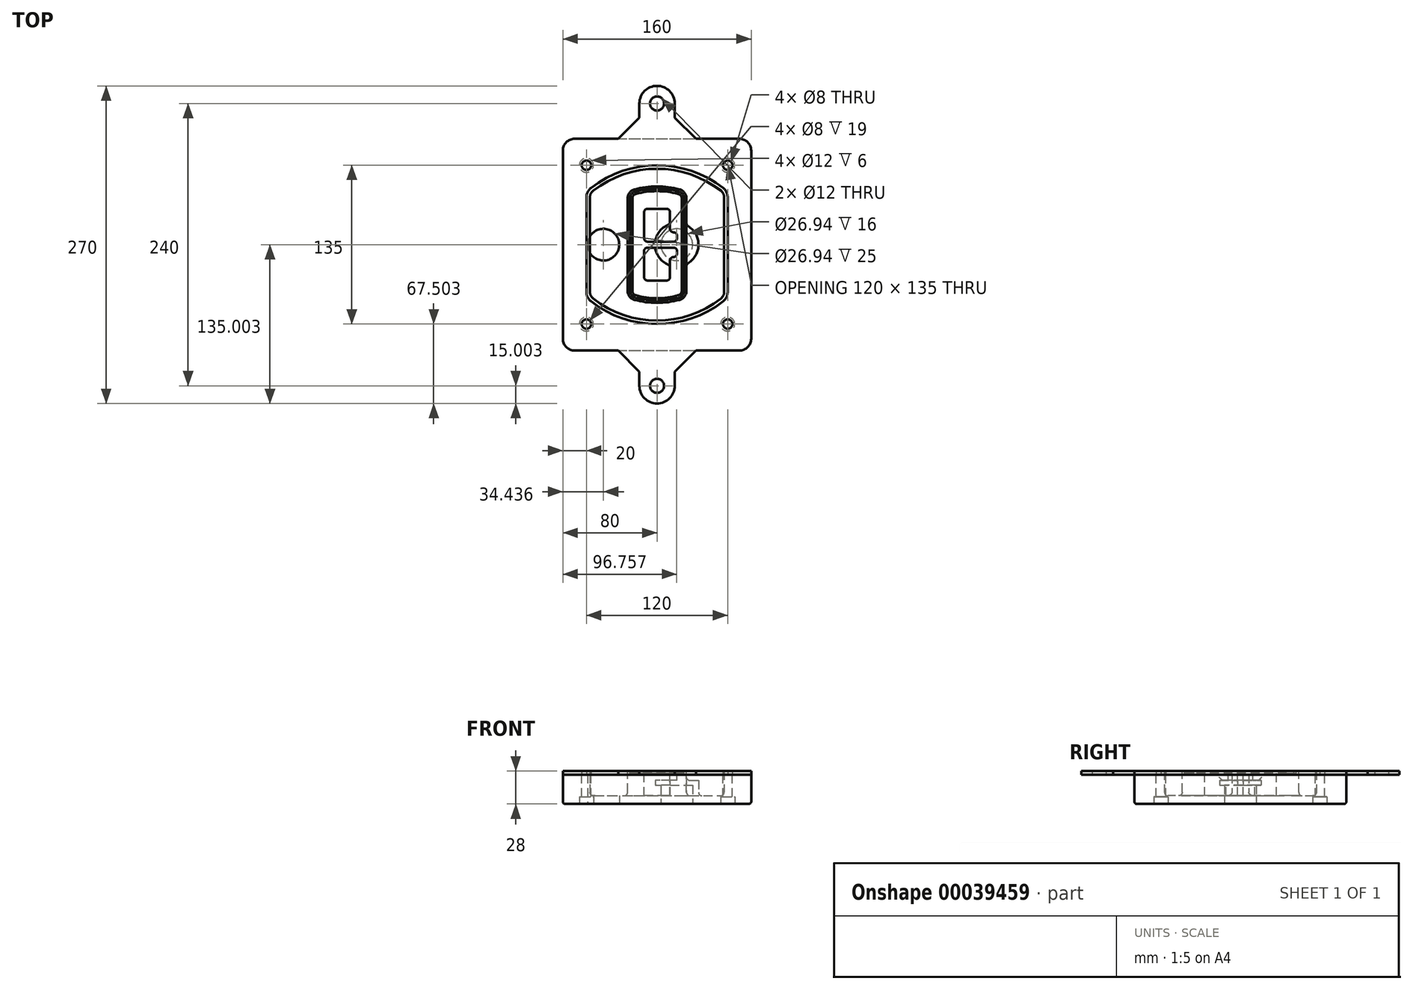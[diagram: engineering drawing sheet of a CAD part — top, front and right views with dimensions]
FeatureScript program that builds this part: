
annotation { "Feature Type Name" : "Feature", "Feature Type Description" : "" }
export const myFeature = defineFeature(function(context is Context, id is Id, definition is map)
    precondition{}
    {
        {
            var Q0;
            Q0=qCreatedBy(makeId("Top.planeOp"),FACE);
            var sketch = newSketch(context, id + "F0", { "sketchPlane" : qUnion([Q0])});
            skPoint(sketch, "E0.rect.middle", {"position": v(0, 0) * mm});
            skLineSegment(sketch, "E1.bottom", {"start": v(24.05, 28.38) * mm, "end": v(164.05, 28.38) * mm});
            skLineSegment(sketch, "E1.top", {"start": v(24.05, 208.38) * mm, "end": v(164.05, 208.38) * mm});
            skLineSegment(sketch, "E1.left", {"start": v(14.05, 38.38) * mm, "end": v(14.05, 198.38) * mm});
            skLineSegment(sketch, "E1.right", {"start": v(174.05, 38.38) * mm, "end": v(174.05, 198.38) * mm});
            skLineSegment(sketch, "E2", {"start": v(14.05, 208.38) * mm, "end": v(174.05, 28.38) * mm, "construction": true});
            skLineSegment(sketch, "E3", {"start": v(174.05, 208.38) * mm, "end": v(14.05, 28.38) * mm, "construction": true});
            skCircle(sketch, "E4", {"center": v(34.05, 185.88) * mm, "radius": 4 * mm});
            skCircle(sketch, "E5", {"center": v(154.05, 185.88) * mm, "radius": 4 * mm});
            skCircle(sketch, "E6", {"center": v(154.05, 50.88) * mm, "radius": 4 * mm});
            skCircle(sketch, "E7", {"center": v(34.05, 50.88) * mm, "radius": 4 * mm});
            skLineSegment(sketch, "E8", {"start": v(34.05, 185.88) * mm, "end": v(154.05, 185.88) * mm, "construction": true});
            skLineSegment(sketch, "E9", {"start": v(154.05, 185.88) * mm, "end": v(154.05, 50.88) * mm, "construction": true});
            skLineSegment(sketch, "E10", {"start": v(154.05, 50.88) * mm, "end": v(34.05, 50.88) * mm, "construction": true});
            skLineSegment(sketch, "E11", {"start": v(34.05, 50.88) * mm, "end": v(34.05, 185.88) * mm, "construction": true});
            skLineSegment(sketch, "E12", {"start": v(34.05, 158.68) * mm, "end": v(34.05, 78.09) * mm});
            skLineSegment(sketch, "E13", {"start": v(154.05, 158.68) * mm, "end": v(154.05, 78.09) * mm});
            skArc(sketch, "E14", {"start": v(150.2, 166.56) * mm, "mid": v(94.05, 185.88) * mm, "end": v(37.9, 166.56) * mm});
            skArc(sketch, "E15", {"start": v(37.9, 70.2) * mm, "mid": v(94.05, 50.88) * mm, "end": v(150.2, 70.2) * mm});
            skLineSegment(sketch, "E16", {"start": v(34.05, 118.38) * mm, "end": v(154.05, 118.38) * mm, "construction": true});
            skPoint(sketch, "E17.visualSharp", {"position": v(34.05, 73.38) * mm});
            skArc(sketch, "E17.filletArc", {"start": v(34.05, 78.09) * mm, "mid": v(35.06, 73.7) * mm, "end": v(37.9, 70.2) * mm});
            skPoint(sketch, "E18.visualSharp", {"position": v(34.05, 163.38) * mm});
            skArc(sketch, "E18.filletArc", {"start": v(37.9, 166.56) * mm, "mid": v(35.06, 163.06) * mm, "end": v(34.05, 158.68) * mm});
            skPoint(sketch, "E19.visualSharp", {"position": v(154.05, 163.38) * mm});
            skArc(sketch, "E19.filletArc", {"start": v(154.05, 158.68) * mm, "mid": v(153.04, 163.06) * mm, "end": v(150.2, 166.56) * mm});
            skPoint(sketch, "E20.visualSharp", {"position": v(154.05, 73.38) * mm});
            skArc(sketch, "E20.filletArc", {"start": v(150.2, 70.2) * mm, "mid": v(153.04, 73.7) * mm, "end": v(154.05, 78.09) * mm});
            skPoint(sketch, "E21.visualSharp", {"position": v(14.05, 208.38) * mm});
            skArc(sketch, "E21.filletArc", {"start": v(24.05, 208.38) * mm, "mid": v(16.98, 205.45) * mm, "end": v(14.05, 198.38) * mm});
            skPoint(sketch, "E22.visualSharp", {"position": v(174.05, 208.38) * mm});
            skArc(sketch, "E22.filletArc", {"start": v(174.05, 198.38) * mm, "mid": v(171.12, 205.45) * mm, "end": v(164.05, 208.38) * mm});
            skPoint(sketch, "E23.visualSharp", {"position": v(174.05, 28.38) * mm});
            skArc(sketch, "E23.filletArc", {"start": v(164.05, 28.38) * mm, "mid": v(171.12, 31.31) * mm, "end": v(174.05, 38.38) * mm});
            skPoint(sketch, "E24.visualSharp", {"position": v(14.05, 28.38) * mm});
            skArc(sketch, "E24.filletArc", {"start": v(14.05, 38.38) * mm, "mid": v(16.98, 31.31) * mm, "end": v(24.05, 28.38) * mm});
            skArc(sketch, "E25.0", {"start": v(151.05, 158.68) * mm, "mid": v(150.34, 161.75) * mm, "end": v(148.36, 164.2) * mm});
            skLineSegment(sketch, "E25.1", {"start": v(151.05, 158.68) * mm, "end": v(151.05, 78.09) * mm});
            skArc(sketch, "E25.2", {"start": v(148.36, 72.57) * mm, "mid": v(150.34, 75.02) * mm, "end": v(151.05, 78.09) * mm});
            skArc(sketch, "E25.3", {"start": v(39.74, 72.57) * mm, "mid": v(94.05, 53.88) * mm, "end": v(148.36, 72.57) * mm});
            skArc(sketch, "E25.4", {"start": v(37.05, 78.09) * mm, "mid": v(37.76, 75.02) * mm, "end": v(39.74, 72.57) * mm});
            skArc(sketch, "E25.5", {"start": v(148.36, 164.2) * mm, "mid": v(94.05, 182.88) * mm, "end": v(39.74, 164.2) * mm});
            skLineSegment(sketch, "E25.6", {"start": v(37.05, 158.68) * mm, "end": v(37.05, 78.09) * mm});
            skArc(sketch, "E25.7", {"start": v(39.74, 164.2) * mm, "mid": v(37.76, 161.75) * mm, "end": v(37.05, 158.68) * mm});
            skArc(sketch, "E26.0", {"start": v(35.43, 169.71) * mm, "mid": v(31.47, 164.82) * mm, "end": v(30.05, 158.68) * mm});
            skArc(sketch, "E26.1", {"start": v(152.67, 169.71) * mm, "mid": v(94.05, 189.88) * mm, "end": v(35.43, 169.71) * mm});
            skArc(sketch, "E26.2", {"start": v(158.05, 158.68) * mm, "mid": v(156.63, 164.82) * mm, "end": v(152.67, 169.71) * mm});
            skLineSegment(sketch, "E26.3", {"start": v(158.05, 158.68) * mm, "end": v(158.05, 78.09) * mm});
            skArc(sketch, "E26.4", {"start": v(152.67, 67.05) * mm, "mid": v(156.63, 71.95) * mm, "end": v(158.05, 78.09) * mm});
            skLineSegment(sketch, "E26.5", {"start": v(30.05, 158.68) * mm, "end": v(30.05, 78.09) * mm});
            skArc(sketch, "E26.6", {"start": v(35.43, 67.05) * mm, "mid": v(94.05, 46.88) * mm, "end": v(152.67, 67.05) * mm});
            skArc(sketch, "E26.7", {"start": v(30.05, 78.09) * mm, "mid": v(31.47, 71.95) * mm, "end": v(35.43, 67.05) * mm});
            skSolve(sketch);
        }
        {
            var Q0;
            Q0=makeQuery(id+"F0.imprint","IMPRINT",FACE,{"disambiguationData":[TD([[makeQuery(id+"F0.imprint","IMPRINT",EDGE,{"derivedFrom":sQuery(id+"F0.wireOp",EDGE,"E1.bottom")}),1.0]])]});
            var Q1;
            Q1=makeQuery(id+"F0.imprint","IMPRINT",FACE,{"disambiguationData":[TD([[makeQuery(id+"F0.imprint","IMPRINT",EDGE,{"derivedFrom":sQuery(id+"F0.wireOp",EDGE,"E12")}),1.0]])]});
            var Q2;
            Q2=makeQuery(id+"F0.imprint","IMPRINT",FACE,{"disambiguationData":[TD([[makeQuery(id+"F0.imprint","IMPRINT",EDGE,{"derivedFrom":sQuery(id+"F0.wireOp",EDGE,"E25.0")}),1.0]])]});
            var Q3;
            Q3=makeQuery(id+"F0.imprint","IMPRINT",FACE,{"disambiguationData":[TD([[makeQuery(id+"F0.imprint","IMPRINT",EDGE,{"derivedFrom":sQuery(id+"F0.wireOp",EDGE,"E12")}),-1.0]])]});
            extrude(context, id + "F1", {"entities" : qUnion([Q0, Q1, Q2, Q3]), "oppositeDirection" : true, "depth" : 25 * mm});
        }
        {
            var Q0;
            Q0=makeQuery(id+"F0.imprint","IMPRINT",FACE,{"disambiguationData":[TD([[makeQuery(id+"F0.imprint","IMPRINT",EDGE,{"derivedFrom":sQuery(id+"F0.wireOp",EDGE,"E12")}),1.0]])]});
            extrude(context, id + "F2", {"entities" : qUnion([Q0]), "operationType" : NewBodyOperationType.ADD, "depth" : 3 * mm});
        }
        {
            var Q0;
            Q0=makeQuery(id+"F0.imprint","IMPRINT",FACE,{"disambiguationData":[TD([[makeQuery(id+"F0.imprint","IMPRINT",EDGE,{"derivedFrom":sQuery(id+"F0.wireOp",EDGE,"E25.0")}),1.0]])]});
            extrude(context, id + "F3", {"entities" : qUnion([Q0]), "operationType" : NewBodyOperationType.REMOVE, "oppositeDirection" : true, "depth" : 18 * mm});
        }
        {
            var Q0;
            Q0=makeQuery(id+"F2.opExtrude","CAP_FACE",FACE,{"disambiguationData":[OSD([sQuery(id+"F0.wireOp",EDGE,"E12"),sQuery(id+"F0.wireOp",EDGE,"E13"),sQuery(id+"F0.wireOp",EDGE,"E14"),sQuery(id+"F0.wireOp",EDGE,"E15"),sQuery(id+"F0.wireOp",EDGE,"E17.filletArc"),sQuery(id+"F0.wireOp",EDGE,"E18.filletArc"),sQuery(id+"F0.wireOp",EDGE,"E19.filletArc"),sQuery(id+"F0.wireOp",EDGE,"E20.filletArc"),sQuery(id+"F0.wireOp",EDGE,"E25.0"),sQuery(id+"F0.wireOp",EDGE,"E25.1"),sQuery(id+"F0.wireOp",EDGE,"E25.2"),sQuery(id+"F0.wireOp",EDGE,"E25.3"),sQuery(id+"F0.wireOp",EDGE,"E25.4"),sQuery(id+"F0.wireOp",EDGE,"E25.5"),sQuery(id+"F0.wireOp",EDGE,"E25.6"),sQuery(id+"F0.wireOp",EDGE,"E25.7")])],"isStart":false});
            var sketch = newSketch(context, id + "F4", { "sketchPlane" : qUnion([Q0])});
            skArc(sketch, "E27.0", {"start": v(74.97, 71.41) * mm, "mid": v(94.05, 68.88) * mm, "end": v(113.13, 71.41) * mm});
            skArc(sketch, "E28.0", {"start": v(113.13, 165.35) * mm, "mid": v(94.05, 167.88) * mm, "end": v(74.97, 165.35) * mm});
            skLineSegment(sketch, "E29", {"start": v(69.05, 157.63) * mm, "end": v(69.05, 79.14) * mm});
            skLineSegment(sketch, "E30", {"start": v(119.05, 157.63) * mm, "end": v(119.05, 79.14) * mm});
            skLineSegment(sketch, "E31", {"start": v(69.05, 163.48) * mm, "end": v(119.05, 163.48) * mm, "construction": true});
            skLineSegment(sketch, "E32", {"start": v(69.05, 73.28) * mm, "end": v(119.05, 73.28) * mm, "construction": true});
            skPoint(sketch, "E33.visualSharp", {"position": v(69.05, 163.48) * mm});
            skArc(sketch, "E33.filletArc", {"start": v(74.97, 165.35) * mm, "mid": v(70.7, 162.5) * mm, "end": v(69.05, 157.63) * mm});
            skPoint(sketch, "E34.visualSharp", {"position": v(119.05, 163.48) * mm});
            skArc(sketch, "E34.filletArc", {"start": v(119.05, 157.63) * mm, "mid": v(117.4, 162.5) * mm, "end": v(113.13, 165.35) * mm});
            skPoint(sketch, "E35.visualSharp", {"position": v(119.05, 73.28) * mm});
            skArc(sketch, "E35.filletArc", {"start": v(113.13, 71.41) * mm, "mid": v(117.4, 74.27) * mm, "end": v(119.05, 79.14) * mm});
            skPoint(sketch, "E36.visualSharp", {"position": v(69.05, 73.28) * mm});
            skArc(sketch, "E36.filletArc", {"start": v(69.05, 79.14) * mm, "mid": v(70.7, 74.27) * mm, "end": v(74.97, 71.41) * mm});
            skArc(sketch, "E37.0", {"start": v(148.36, 164.2) * mm, "mid": v(94.05, 182.88) * mm, "end": v(39.74, 164.2) * mm});
            skArc(sketch, "E37.1", {"start": v(39.74, 164.2) * mm, "mid": v(37.76, 161.75) * mm, "end": v(37.05, 158.68) * mm});
            skLineSegment(sketch, "E37.2", {"start": v(37.05, 158.68) * mm, "end": v(37.05, 78.09) * mm});
            skArc(sketch, "E37.3", {"start": v(37.05, 78.09) * mm, "mid": v(37.76, 75.02) * mm, "end": v(39.74, 72.57) * mm});
            skArc(sketch, "E37.4", {"start": v(39.74, 72.57) * mm, "mid": v(94.05, 53.88) * mm, "end": v(148.36, 72.57) * mm});
            skArc(sketch, "E37.5", {"start": v(148.36, 72.57) * mm, "mid": v(150.34, 75.02) * mm, "end": v(151.05, 78.09) * mm});
            skLineSegment(sketch, "E37.6", {"start": v(151.05, 158.68) * mm, "end": v(151.05, 78.09) * mm});
            skArc(sketch, "E37.7", {"start": v(151.05, 158.68) * mm, "mid": v(150.34, 161.75) * mm, "end": v(148.36, 164.2) * mm});
            skLineSegment(sketch, "E38.0", {"start": v(117.05, 157.63) * mm, "end": v(117.05, 79.14) * mm});
            skArc(sketch, "E38.1", {"start": v(112.61, 73.34) * mm, "mid": v(115.81, 75.49) * mm, "end": v(117.05, 79.14) * mm});
            skArc(sketch, "E38.2", {"start": v(75.49, 73.34) * mm, "mid": v(94.05, 70.88) * mm, "end": v(112.61, 73.34) * mm});
            skArc(sketch, "E38.3", {"start": v(71.05, 79.14) * mm, "mid": v(72.29, 75.49) * mm, "end": v(75.49, 73.34) * mm});
            skLineSegment(sketch, "E38.4", {"start": v(71.05, 157.63) * mm, "end": v(71.05, 79.14) * mm});
            skArc(sketch, "E38.5", {"start": v(117.05, 157.63) * mm, "mid": v(115.81, 161.28) * mm, "end": v(112.61, 163.42) * mm});
            skArc(sketch, "E38.6", {"start": v(75.49, 163.42) * mm, "mid": v(72.29, 161.28) * mm, "end": v(71.05, 157.63) * mm});
            skArc(sketch, "E38.7", {"start": v(112.61, 163.42) * mm, "mid": v(94.05, 165.88) * mm, "end": v(75.49, 163.42) * mm});
            skArc(sketch, "E39.0", {"start": v(115.05, 157.63) * mm, "mid": v(114.23, 160.06) * mm, "end": v(112.1, 161.5) * mm});
            skLineSegment(sketch, "E39.1", {"start": v(115.05, 157.63) * mm, "end": v(115.05, 79.14) * mm});
            skArc(sketch, "E39.2", {"start": v(112.1, 75.27) * mm, "mid": v(114.23, 76.7) * mm, "end": v(115.05, 79.14) * mm});
            skArc(sketch, "E39.3", {"start": v(76, 75.27) * mm, "mid": v(94.05, 72.88) * mm, "end": v(112.1, 75.27) * mm});
            skArc(sketch, "E39.4", {"start": v(73.05, 79.14) * mm, "mid": v(73.87, 76.7) * mm, "end": v(76, 75.27) * mm});
            skArc(sketch, "E39.5", {"start": v(112.1, 161.5) * mm, "mid": v(94.05, 163.88) * mm, "end": v(76, 161.5) * mm});
            skLineSegment(sketch, "E39.6", {"start": v(73.05, 157.63) * mm, "end": v(73.05, 79.14) * mm});
            skArc(sketch, "E39.7", {"start": v(76, 161.5) * mm, "mid": v(73.87, 160.06) * mm, "end": v(73.05, 157.63) * mm});
            skLineSegment(sketch, "E40", {"start": v(69.05, 118.38) * mm, "end": v(119.05, 118.38) * mm, "construction": true});
            skLineSegment(sketch, "E41", {"start": v(83.05, 123.88) * mm, "end": v(83.05, 145.88) * mm});
            skLineSegment(sketch, "E42", {"start": v(86.05, 148.88) * mm, "end": v(102.05, 148.88) * mm});
            skLineSegment(sketch, "E43", {"start": v(105.05, 145.88) * mm, "end": v(105.05, 131.88) * mm});
            skLineSegment(sketch, "E44", {"start": v(108.05, 128.88) * mm, "end": v(108.05, 128.88) * mm});
            skLineSegment(sketch, "E45", {"start": v(111.05, 125.88) * mm, "end": v(111.05, 123.88) * mm});
            skLineSegment(sketch, "E46", {"start": v(108.05, 120.88) * mm, "end": v(86.05, 120.88) * mm});
            skPoint(sketch, "E47.visualSharp", {"position": v(83.05, 148.88) * mm});
            skArc(sketch, "E47.filletArc", {"start": v(86.05, 148.88) * mm, "mid": v(83.93, 148) * mm, "end": v(83.05, 145.88) * mm});
            skPoint(sketch, "E48.visualSharp", {"position": v(105.05, 148.88) * mm});
            skArc(sketch, "E48.filletArc", {"start": v(105.05, 145.88) * mm, "mid": v(104.17, 148) * mm, "end": v(102.05, 148.88) * mm});
            skPoint(sketch, "E49.visualSharp", {"position": v(105.05, 128.88) * mm});
            skArc(sketch, "E49.filletArc", {"start": v(105.05, 131.88) * mm, "mid": v(105.93, 129.76) * mm, "end": v(108.05, 128.88) * mm});
            skPoint(sketch, "E50.visualSharp", {"position": v(111.05, 128.88) * mm});
            skArc(sketch, "E50.filletArc", {"start": v(111.05, 125.88) * mm, "mid": v(110.17, 128) * mm, "end": v(108.05, 128.88) * mm});
            skPoint(sketch, "E51.visualSharp", {"position": v(111.05, 120.88) * mm});
            skArc(sketch, "E51.filletArc", {"start": v(108.05, 120.88) * mm, "mid": v(110.17, 121.76) * mm, "end": v(111.05, 123.88) * mm});
            skPoint(sketch, "E52.visualSharp", {"position": v(83.05, 120.88) * mm});
            skArc(sketch, "E52.filletArc", {"start": v(83.05, 123.88) * mm, "mid": v(83.93, 121.76) * mm, "end": v(86.05, 120.88) * mm});
            skLineSegment(sketch, "E53.0.MirrorCS", {"start": v(108.05, 115.88) * mm, "end": v(86.05, 115.88) * mm});
            skArc(sketch, "E54.0.MirrorCS", {"start": v(83.05, 112.88) * mm, "mid": v(83.93, 115) * mm, "end": v(86.05, 115.88) * mm});
            skLineSegment(sketch, "E55.0.MirrorCS", {"start": v(83.05, 112.88) * mm, "end": v(83.05, 90.88) * mm});
            skArc(sketch, "E56.0.MirrorCS", {"start": v(86.05, 87.88) * mm, "mid": v(83.93, 88.76) * mm, "end": v(83.05, 90.88) * mm});
            skLineSegment(sketch, "E57.0.MirrorCS", {"start": v(86.05, 87.88) * mm, "end": v(102.05, 87.88) * mm});
            skArc(sketch, "E58.0.MirrorCS", {"start": v(105.05, 90.88) * mm, "mid": v(104.17, 88.76) * mm, "end": v(102.05, 87.88) * mm});
            skLineSegment(sketch, "E59.0.MirrorCS", {"start": v(105.05, 90.88) * mm, "end": v(105.05, 104.88) * mm});
            skArc(sketch, "E60.0.MirrorCS", {"start": v(105.05, 104.88) * mm, "mid": v(105.93, 107) * mm, "end": v(108.05, 107.88) * mm});
            skArc(sketch, "E61.0.MirrorCS", {"start": v(111.05, 110.88) * mm, "mid": v(110.17, 108.76) * mm, "end": v(108.05, 107.88) * mm});
            skLineSegment(sketch, "E62.0.MirrorCS", {"start": v(111.05, 110.88) * mm, "end": v(111.05, 112.88) * mm});
            skArc(sketch, "E63.0.MirrorCS", {"start": v(108.05, 115.88) * mm, "mid": v(110.17, 115) * mm, "end": v(111.05, 112.88) * mm});
            skSolve(sketch);
        }
        {
            var Q0;
            Q0=makeQuery(id+"F4.imprint","IMPRINT",FACE,{"disambiguationData":[TD([[makeQuery(id+"F4.imprint","IMPRINT",EDGE,{"derivedFrom":sQuery(id+"F4.wireOp",EDGE,"E27.0")}),1.0]])]});
            var Q1;
            Q1=makeQuery(id+"F4.imprint","IMPRINT",FACE,{"disambiguationData":[TD([[makeQuery(id+"F4.imprint","IMPRINT",EDGE,{"derivedFrom":sQuery(id+"F4.wireOp",EDGE,"E38.0")}),-1.0]])]});
            var Q2;
            Q2=makeQuery(id+"F4.imprint","IMPRINT",FACE,{"disambiguationData":[TD([[makeQuery(id+"F4.imprint","IMPRINT",EDGE,{"derivedFrom":sQuery(id+"F4.wireOp",EDGE,"E39.0")}),1.0]])]});
            extrude(context, id + "F5", {"entities" : qUnion([Q0, Q1, Q2]), "operationType" : NewBodyOperationType.ADD, "endBound" : BoundingType.UP_TO_NEXT, "oppositeDirection" : true, "depth" : 25 * mm});
        }
        {
            var Q0;
            Q0=makeQuery(id+"F4.imprint","IMPRINT",FACE,{"disambiguationData":[TD([[makeQuery(id+"F4.imprint","IMPRINT",EDGE,{"derivedFrom":sQuery(id+"F4.wireOp",EDGE,"E38.0")}),-1.0]])]});
            extrude(context, id + "F6", {"entities" : qUnion([Q0]), "operationType" : NewBodyOperationType.REMOVE, "oppositeDirection" : true, "depth" : 2 * mm});
        }
        {
            var Q0;
            Q0=makeQuery(id+"F1.opExtrude","CAP_FACE",FACE,{"disambiguationData":[OSD([sQuery(id+"F0.wireOp",EDGE,"E1.bottom"),sQuery(id+"F0.wireOp",EDGE,"E1.top"),sQuery(id+"F0.wireOp",EDGE,"E1.left"),sQuery(id+"F0.wireOp",EDGE,"E1.right"),sQuery(id+"F0.wireOp",EDGE,"E4"),sQuery(id+"F0.wireOp",EDGE,"E5"),sQuery(id+"F0.wireOp",EDGE,"E6"),sQuery(id+"F0.wireOp",EDGE,"E7"),sQuery(id+"F0.wireOp",EDGE,"E21.filletArc"),sQuery(id+"F0.wireOp",EDGE,"E22.filletArc"),sQuery(id+"F0.wireOp",EDGE,"E23.filletArc"),sQuery(id+"F0.wireOp",EDGE,"E24.filletArc")])],"isStart":false});
            var sketch = newSketch(context, id + "F7", { "sketchPlane" : qUnion([Q0])});
            skCircle(sketch, "E64", {"center": v(110.8, -118.38) * mm, "radius": 13.47 * mm});
            skCircle(sketch, "E65", {"center": v(48.49, -118.38) * mm, "radius": 13.47 * mm});
            skLineSegment(sketch, "E66", {"start": v(174.05, -118.38) * mm, "end": v(14.05, -118.38) * mm});
            skCircle(sketch, "E67", {"center": v(110.8, -118.38) * mm, "radius": 18.47 * mm});
            skCircle(sketch, "E68", {"center": v(154.05, -185.88) * mm, "radius": 6 * mm});
            skCircle(sketch, "E69", {"center": v(34.05, -185.88) * mm, "radius": 6 * mm});
            skCircle(sketch, "E70", {"center": v(34.05, -50.88) * mm, "radius": 6 * mm});
            skCircle(sketch, "E71", {"center": v(154.05, -50.88) * mm, "radius": 6 * mm});
            skSolve(sketch);
        }
        {
            var Q0;
            {var subQ1=sQuery(id+"F7.wireOp",EDGE,"E66");var subQ4=sQuery(id+"F7.wireOp",EDGE,"E64");var subQ6=makeQuery(id+"F7.imprint","INTERSECT",VERTEX,{"disambiguationData":[OD(0.0)],"derivedFrom":[subQ4,subQ1]});Q0=makeQuery(id+"F7.imprint","IMPRINT",FACE,{"disambiguationData":[TD([[makeQuery(id+"F7.imprint","IMPRINT",EDGE,{"disambiguationData":[TD([[subQ6,-1.0]])],"derivedFrom":subQ4}),-1.0]])]});}
            var Q1;
            {var subQ0=sQuery(id+"F7.wireOp",EDGE,"E66");var subQ1=sQuery(id+"F7.wireOp",EDGE,"E64");var subQ3=makeQuery(id+"F7.imprint","INTERSECT",VERTEX,{"disambiguationData":[OD(0.0)],"derivedFrom":[subQ1,subQ0]});Q1=makeQuery(id+"F7.imprint","IMPRINT",FACE,{"disambiguationData":[TD([[makeQuery(id+"F7.imprint","IMPRINT",EDGE,{"disambiguationData":[TD([[subQ3,-1.0]])],"derivedFrom":subQ1}),1.0]])]});}
            var Q2;
            {var subQ0=sQuery(id+"F7.wireOp",EDGE,"E66");var subQ1=sQuery(id+"F7.wireOp",EDGE,"E64");var subQ3=makeQuery(id+"F7.imprint","INTERSECT",VERTEX,{"disambiguationData":[OD(0.0)],"derivedFrom":[subQ1,subQ0]});Q2=makeQuery(id+"F7.imprint","IMPRINT",FACE,{"disambiguationData":[TD([[makeQuery(id+"F7.imprint","IMPRINT",EDGE,{"disambiguationData":[TD([[subQ3,1.0]])],"derivedFrom":subQ1}),1.0]])]});}
            var Q3;
            {var subQ1=sQuery(id+"F7.wireOp",EDGE,"E66");var subQ4=sQuery(id+"F7.wireOp",EDGE,"E64");var subQ6=makeQuery(id+"F7.imprint","INTERSECT",VERTEX,{"disambiguationData":[OD(0.0)],"derivedFrom":[subQ4,subQ1]});Q3=makeQuery(id+"F7.imprint","IMPRINT",FACE,{"disambiguationData":[TD([[makeQuery(id+"F7.imprint","IMPRINT",EDGE,{"disambiguationData":[TD([[subQ6,1.0]])],"derivedFrom":subQ4}),-1.0]])]});}
            extrude(context, id + "F8", {"entities" : qUnion([Q0, Q1, Q2, Q3]), "operationType" : NewBodyOperationType.ADD, "oppositeDirection" : true, "depth" : 20 * mm});
        }
        {
            var Q0;
            {var subQ0=sQuery(id+"F7.wireOp",EDGE,"E66");var subQ1=sQuery(id+"F7.wireOp",EDGE,"E64");var subQ3=makeQuery(id+"F7.imprint","INTERSECT",VERTEX,{"disambiguationData":[OD(0.0)],"derivedFrom":[subQ1,subQ0]});Q0=makeQuery(id+"F7.imprint","IMPRINT",FACE,{"disambiguationData":[TD([[makeQuery(id+"F7.imprint","IMPRINT",EDGE,{"disambiguationData":[TD([[subQ3,-1.0]])],"derivedFrom":subQ1}),1.0]])]});}
            var Q1;
            {var subQ0=sQuery(id+"F7.wireOp",EDGE,"E66");var subQ1=sQuery(id+"F7.wireOp",EDGE,"E64");var subQ3=makeQuery(id+"F7.imprint","INTERSECT",VERTEX,{"disambiguationData":[OD(0.0)],"derivedFrom":[subQ1,subQ0]});Q1=makeQuery(id+"F7.imprint","IMPRINT",FACE,{"disambiguationData":[TD([[makeQuery(id+"F7.imprint","IMPRINT",EDGE,{"disambiguationData":[TD([[subQ3,1.0]])],"derivedFrom":subQ1}),1.0]])]});}
            extrude(context, id + "F9", {"entities" : qUnion([Q0, Q1]), "operationType" : NewBodyOperationType.REMOVE, "oppositeDirection" : true, "depth" : 16 * mm});
        }
        {
            var Q0;
            {var subQ0=sQuery(id+"F7.wireOp",EDGE,"E66");var subQ1=sQuery(id+"F7.wireOp",EDGE,"E65");var subQ3=makeQuery(id+"F7.imprint","INTERSECT",VERTEX,{"disambiguationData":[OD(0.0)],"derivedFrom":[subQ1,subQ0]});Q0=makeQuery(id+"F7.imprint","IMPRINT",FACE,{"disambiguationData":[TD([[makeQuery(id+"F7.imprint","IMPRINT",EDGE,{"disambiguationData":[TD([[subQ3,-1.0]])],"derivedFrom":subQ1}),1.0]])]});}
            var Q1;
            {var subQ0=sQuery(id+"F7.wireOp",EDGE,"E66");var subQ1=sQuery(id+"F7.wireOp",EDGE,"E65");var subQ3=makeQuery(id+"F7.imprint","INTERSECT",VERTEX,{"disambiguationData":[OD(0.0)],"derivedFrom":[subQ1,subQ0]});Q1=makeQuery(id+"F7.imprint","IMPRINT",FACE,{"disambiguationData":[TD([[makeQuery(id+"F7.imprint","IMPRINT",EDGE,{"disambiguationData":[TD([[subQ3,1.0]])],"derivedFrom":subQ1}),1.0]])]});}
            extrude(context, id + "F10", {"entities" : qUnion([Q0, Q1]), "operationType" : NewBodyOperationType.REMOVE, "oppositeDirection" : true, "depth" : 25 * mm});
        }
        {
            var Q0;
            Q0=makeQuery(id+"F7.imprint","IMPRINT",FACE,{"disambiguationData":[TD([[makeQuery(id+"F7.imprint","IMPRINT",EDGE,{"derivedFrom":sQuery(id+"F7.wireOp",EDGE,"E68")}),1.0]])]});
            var Q1;
            Q1=makeQuery(id+"F7.imprint","IMPRINT",FACE,{"disambiguationData":[TD([[makeQuery(id+"F7.imprint","IMPRINT",EDGE,{"derivedFrom":makeQuery(id+"F1.opExtrude","CAP_EDGE",EDGE,{"disambiguationData":[OSD([sQuery(id+"F0.wireOp",EDGE,"E5")])],"isStart":false})}),-1.0]])]});
            var Q2;
            Q2=makeQuery(id+"F7.imprint","IMPRINT",FACE,{"disambiguationData":[TD([[makeQuery(id+"F7.imprint","IMPRINT",EDGE,{"derivedFrom":sQuery(id+"F7.wireOp",EDGE,"E69")}),1.0]])]});
            var Q3;
            Q3=makeQuery(id+"F7.imprint","IMPRINT",FACE,{"disambiguationData":[TD([[makeQuery(id+"F7.imprint","IMPRINT",EDGE,{"derivedFrom":makeQuery(id+"F1.opExtrude","CAP_EDGE",EDGE,{"disambiguationData":[OSD([sQuery(id+"F0.wireOp",EDGE,"E4")])],"isStart":false})}),-1.0]])]});
            var Q4;
            Q4=makeQuery(id+"F7.imprint","IMPRINT",FACE,{"disambiguationData":[TD([[makeQuery(id+"F7.imprint","IMPRINT",EDGE,{"derivedFrom":sQuery(id+"F7.wireOp",EDGE,"E70")}),1.0]])]});
            var Q5;
            Q5=makeQuery(id+"F7.imprint","IMPRINT",FACE,{"disambiguationData":[TD([[makeQuery(id+"F7.imprint","IMPRINT",EDGE,{"derivedFrom":makeQuery(id+"F1.opExtrude","CAP_EDGE",EDGE,{"disambiguationData":[OSD([sQuery(id+"F0.wireOp",EDGE,"E7")])],"isStart":false})}),-1.0]])]});
            var Q6;
            Q6=makeQuery(id+"F7.imprint","IMPRINT",FACE,{"disambiguationData":[TD([[makeQuery(id+"F7.imprint","IMPRINT",EDGE,{"derivedFrom":sQuery(id+"F7.wireOp",EDGE,"E71")}),1.0]])]});
            var Q7;
            Q7=makeQuery(id+"F7.imprint","IMPRINT",FACE,{"disambiguationData":[TD([[makeQuery(id+"F7.imprint","IMPRINT",EDGE,{"derivedFrom":makeQuery(id+"F1.opExtrude","CAP_EDGE",EDGE,{"disambiguationData":[OSD([sQuery(id+"F0.wireOp",EDGE,"E6")])],"isStart":false})}),-1.0]])]});
            extrude(context, id + "F11", {"entities" : qUnion([Q0, Q1, Q2, Q3, Q4, Q5, Q6, Q7]), "operationType" : NewBodyOperationType.REMOVE, "oppositeDirection" : true, "depth" : 6 * mm});
        }
        {
            var Q0;
            Q0=makeQuery(id+"F9.boolean.opBoolean","COPY",FACE,{"derivedFrom":makeQuery(id+"F9.opExtrude","CAP_FACE",FACE,{"disambiguationData":[OSD([sQuery(id+"F7.wireOp",EDGE,"E64")])],"isStart":false})});
            var sketch = newSketch(context, id + "F12", { "sketchPlane" : qUnion([Q0])});
            skArc(sketch, "E72.0", {"start": v(105.05, -100.83) * mm, "mid": v(96.62, -106.56) * mm, "end": v(92.5, -115.88) * mm});
            skArc(sketch, "E72.1", {"start": v(92.5, -120.88) * mm, "mid": v(96.62, -130.2) * mm, "end": v(105.05, -135.93) * mm});
            skLineSegment(sketch, "E73", {"start": v(92.5, -120.88) * mm, "end": v(108.05, -120.88) * mm});
            skLineSegment(sketch, "E74.0", {"start": v(108.05, -115.88) * mm, "end": v(92.5, -115.88) * mm});
            skArc(sketch, "E74.1", {"start": v(108.05, -115.88) * mm, "mid": v(110.17, -115) * mm, "end": v(111.05, -112.88) * mm});
            skLineSegment(sketch, "E74.2", {"start": v(111.05, -110.88) * mm, "end": v(111.05, -112.88) * mm});
            skArc(sketch, "E74.3", {"start": v(111.05, -110.88) * mm, "mid": v(110.17, -108.76) * mm, "end": v(108.05, -107.88) * mm});
            skArc(sketch, "E74.4", {"start": v(105.05, -104.88) * mm, "mid": v(105.93, -107) * mm, "end": v(108.05, -107.88) * mm});
            skLineSegment(sketch, "E74.5", {"start": v(105.05, -100.83) * mm, "end": v(105.05, -104.88) * mm});
            skLineSegment(sketch, "E74.7", {"start": v(108.05, -120.88) * mm, "end": v(92.5, -120.88) * mm});
            skArc(sketch, "E74.8", {"start": v(108.05, -120.88) * mm, "mid": v(110.17, -121.76) * mm, "end": v(111.05, -123.88) * mm});
            skLineSegment(sketch, "E74.9", {"start": v(111.05, -125.88) * mm, "end": v(111.05, -123.88) * mm});
            skArc(sketch, "E74.10", {"start": v(111.05, -125.88) * mm, "mid": v(110.17, -128) * mm, "end": v(108.05, -128.88) * mm});
            skArc(sketch, "E74.11", {"start": v(105.05, -131.88) * mm, "mid": v(105.93, -129.76) * mm, "end": v(108.05, -128.88) * mm});
            skLineSegment(sketch, "E74.12", {"start": v(105.05, -135.93) * mm, "end": v(105.05, -131.88) * mm});
            skPoint(sketch, "E75.orphan", {"position": v(105.05, -145.88) * mm});
            skPoint(sketch, "E76.orphan", {"position": v(86.05, -120.88) * mm});
            skPoint(sketch, "E77.orphan", {"position": v(86.05, -115.88) * mm});
            skPoint(sketch, "E78.orphan", {"position": v(105.05, -90.88) * mm});
            skSolve(sketch);
        }
        {
            var Q0;
            {var subQ7=sQuery(id+"F12.wireOp",EDGE,"E72.0");var subQ14=sQuery(id+"F12.wireOp",EDGE,"E72.1");var subQ16=sQuery(id+"F12.wireOp",EDGE,"E74.1");var subQ18=sQuery(id+"F12.wireOp",EDGE,"E74.8");Q0=qUnion([makeQuery(id+"F12.imprint","IMPRINT",FACE,{"disambiguationData":[TD([[makeQuery(id+"F12.imprint","IMPRINT",EDGE,{"derivedFrom":subQ7}),1.0]])]}),makeQuery(id+"F12.imprint","IMPRINT",FACE,{"disambiguationData":[TD([[makeQuery(id+"F12.imprint","IMPRINT",EDGE,{"derivedFrom":subQ14}),1.0]])]}),makeQuery(id+"F12.imprint","IMPRINT",FACE,{"disambiguationData":[TD([[makeQuery(id+"F12.imprint","IMPRINT",EDGE,{"derivedFrom":subQ16}),1.0]])]}),makeQuery(id+"F12.imprint","IMPRINT",FACE,{"disambiguationData":[TD([[makeQuery(id+"F12.imprint","IMPRINT",EDGE,{"derivedFrom":subQ18}),-1.0]])]})]);}
            var Q1;
            Q1=makeQuery(id+"F5.boolean.opBoolean","SPLIT",FACE,{"disambiguationData":[TD([makeQuery(id+"F5.opExtrude","SWEPT_FACE",FACE,{"disambiguationData":[OSD([sQuery(id+"F4.wireOp",EDGE,"E41")])]})])],"derivedFrom":makeQuery(id+"F3.boolean.opBoolean","COPY",FACE,{"derivedFrom":makeQuery(id+"F3.opExtrude","CAP_FACE",FACE,{"disambiguationData":[OSD([sQuery(id+"F0.wireOp",EDGE,"E25.0"),sQuery(id+"F0.wireOp",EDGE,"E25.1"),sQuery(id+"F0.wireOp",EDGE,"E25.2"),sQuery(id+"F0.wireOp",EDGE,"E25.3"),sQuery(id+"F0.wireOp",EDGE,"E25.4"),sQuery(id+"F0.wireOp",EDGE,"E25.5"),sQuery(id+"F0.wireOp",EDGE,"E25.6"),sQuery(id+"F0.wireOp",EDGE,"E25.7")])],"isStart":false})})});
            extrude(context, id + "F13", {"entities" : qUnion([Q0]), "operationType" : NewBodyOperationType.REMOVE, "endBound" : BoundingType.UP_TO_SURFACE, "endBoundEntityFace" : qUnion([Q1]), "depth" : 25 * mm});
        }
        {
            var Q0;
            Q0=makeQuery(id+"F3.boolean.opBoolean","COPY",EDGE,{"derivedFrom":makeQuery(id+"F3.opExtrude","CAP_EDGE",EDGE,{"disambiguationData":[OSD([sQuery(id+"F0.wireOp",EDGE,"E25.6")])],"isStart":false})});
            var Q1;
            Q1=makeQuery(id+"F8.boolean.opBoolean","INTERSECT",EDGE,{"derivedFrom":[makeQuery(id+"F5.opExtrude","SWEPT_FACE",FACE,{"disambiguationData":[OSD([sQuery(id+"F4.wireOp",EDGE,"E30")])]}),makeQuery(id+"F8.opExtrude","CAP_FACE",FACE,{"disambiguationData":[OSD([sQuery(id+"F7.wireOp",EDGE,"E67")])],"isStart":false})]});
            var Q2;
            Q2=makeQuery(id+"F8.boolean.opBoolean","INTERSECT",EDGE,{"disambiguationData":[OD(1.0)],"derivedFrom":[makeQuery(id+"F5.opExtrude","SWEPT_FACE",FACE,{"disambiguationData":[OSD([sQuery(id+"F4.wireOp",EDGE,"E30")])]}),makeQuery(id+"F8.opExtrude","SWEPT_FACE",FACE,{"disambiguationData":[OSD([sQuery(id+"F7.wireOp",EDGE,"E67")])]})]});
            var Q3;
            {var subQ0=sQuery(id+"F4.wireOp",EDGE,"E30");Q3=makeQuery(id+"F8.boolean.opBoolean","SPLIT",EDGE,{"disambiguationData":[TD([makeQuery(id+"F5.opExtrude","SWEPT_FACE",FACE,{"disambiguationData":[OSD([sQuery(id+"F4.wireOp",EDGE,"E35.filletArc")])]})])],"derivedFrom":makeQuery(id+"F5.opExtrude","CAP_EDGE",EDGE,{"disambiguationData":[OSD([subQ0])],"isStart":false})});}
            var Q4;
            {var subQ0=sQuery(id+"F0.wireOp",EDGE,"E25.7");var subQ1=sQuery(id+"F0.wireOp",EDGE,"E25.1");var subQ2=sQuery(id+"F0.wireOp",EDGE,"E25.6");var subQ3=sQuery(id+"F0.wireOp",EDGE,"E25.5");var subQ4=sQuery(id+"F0.wireOp",EDGE,"E25.4");var subQ5=sQuery(id+"F0.wireOp",EDGE,"E25.0");var subQ6=sQuery(id+"F0.wireOp",EDGE,"E25.2");var subQ7=sQuery(id+"F0.wireOp",EDGE,"E25.3");Q4=makeQuery(id+"F8.boolean.opBoolean","INTERSECT",EDGE,{"derivedFrom":[makeQuery(id+"F5.boolean.opBoolean","SPLIT",FACE,{"disambiguationData":[TD([makeQuery(id+"F2.opExtrude","SWEPT_FACE",FACE,{"disambiguationData":[OSD([subQ5])]})])],"derivedFrom":makeQuery(id+"F3.boolean.opBoolean","COPY",FACE,{"derivedFrom":makeQuery(id+"F3.opExtrude","CAP_FACE",FACE,{"disambiguationData":[OSD([subQ5,subQ1,subQ6,subQ7,subQ4,subQ3,subQ2,subQ0])],"isStart":false})})}),makeQuery(id+"F8.opExtrude","SWEPT_FACE",FACE,{"disambiguationData":[OSD([sQuery(id+"F7.wireOp",EDGE,"E67")])]})]});}
            var Q5;
            Q5=makeQuery(id+"F8.boolean.opBoolean","INTERSECT",EDGE,{"disambiguationData":[OD(0.0)],"derivedFrom":[makeQuery(id+"F5.opExtrude","SWEPT_FACE",FACE,{"disambiguationData":[OSD([sQuery(id+"F4.wireOp",EDGE,"E30")])]}),makeQuery(id+"F8.opExtrude","SWEPT_FACE",FACE,{"disambiguationData":[OSD([sQuery(id+"F7.wireOp",EDGE,"E67")])]})]});
            fillet(context, id + "F14", {"entities" : qUnion([Q0, Q1, Q2, Q3, Q4, Q5]), "radius" : 3 * mm, "tangentPropagation" : true, "allowEdgeOverflow" : false});
        }
        {
            var Q0;
            Q0=makeQuery(id+"F1.opExtrude","CAP_EDGE",EDGE,{"disambiguationData":[OSD([sQuery(id+"F0.wireOp",EDGE,"E1.bottom")])],"isStart":false});
            fillet(context, id + "F15", {"entities" : qUnion([Q0]), "radius" : 2 * mm, "tangentPropagation" : true, "allowEdgeOverflow" : false});
        }
        {
            var Q0;
            {var subQ0=sQuery(id+"F0.wireOp",EDGE,"E1.bottom");var subQ1=sQuery(id+"F0.wireOp",EDGE,"E1.top");var subQ2=sQuery(id+"F0.wireOp",EDGE,"E1.left");var subQ3=sQuery(id+"F0.wireOp",EDGE,"E1.right");var subQ4=sQuery(id+"F0.wireOp",EDGE,"E4");var subQ5=sQuery(id+"F0.wireOp",EDGE,"E5");var subQ6=sQuery(id+"F0.wireOp",EDGE,"E6");var subQ7=sQuery(id+"F0.wireOp",EDGE,"E7");var subQ8=sQuery(id+"F0.wireOp",EDGE,"E21.filletArc");var subQ9=sQuery(id+"F0.wireOp",EDGE,"E22.filletArc");var subQ10=sQuery(id+"F0.wireOp",EDGE,"E23.filletArc");var subQ11=sQuery(id+"F0.wireOp",EDGE,"E24.filletArc");Q0=makeQuery(id+"F2.boolean.opBoolean","SPLIT",FACE,{"disambiguationData":[TD([makeQuery(id+"F1.opExtrude","SWEPT_FACE",FACE,{"disambiguationData":[OSD([subQ0])]})])],"derivedFrom":makeQuery(id+"F1.opExtrude","CAP_FACE",FACE,{"disambiguationData":[OSD([subQ0,subQ1,subQ2,subQ3,subQ4,subQ5,subQ6,subQ7,subQ8,subQ9,subQ10,subQ11])],"isStart":true})});}
            var sketch = newSketch(context, id + "F16", { "sketchPlane" : qUnion([Q0])});
            skLineSegment(sketch, "E79", {"start": v(94.05, 208.38) * mm, "end": v(94.05, 238.38) * mm});
            skCircle(sketch, "E80", {"center": v(94.05, 238.38) * mm, "radius": 6 * mm});
            skArc(sketch, "E81", {"start": v(109.05, 238.38) * mm, "mid": v(94.05, 253.38) * mm, "end": v(79.05, 238.38) * mm});
            skLineSegment(sketch, "E82", {"start": v(79.05, 238.38) * mm, "end": v(79.05, 226.38) * mm});
            skLineSegment(sketch, "E83", {"start": v(109.05, 238.38) * mm, "end": v(109.05, 226.38) * mm});
            skLineSegment(sketch, "E84", {"start": v(61.05, 208.38) * mm, "end": v(79.05, 226.38) * mm});
            skLineSegment(sketch, "E85", {"start": v(109.05, 226.38) * mm, "end": v(127.05, 208.38) * mm});
            skLineSegment(sketch, "E86", {"start": v(14.05, 118.38) * mm, "end": v(174.05, 118.38) * mm, "construction": true});
            skLineSegment(sketch, "E87.MirrorCS", {"start": v(109.05, -1.62) * mm, "end": v(109.05, 10.38) * mm});
            skArc(sketch, "E88.MirrorCS", {"start": v(109.05, -1.62) * mm, "mid": v(94.05, -16.62) * mm, "end": v(79.05, -1.62) * mm});
            skLineSegment(sketch, "E89.MirrorCS", {"start": v(61.05, 28.38) * mm, "end": v(79.05, 10.38) * mm});
            skCircle(sketch, "E90.MirrorC", {"center": v(94.05, -1.62) * mm, "radius": 6 * mm});
            skLineSegment(sketch, "E91.MirrorCS", {"start": v(109.05, 10.38) * mm, "end": v(127.05, 28.38) * mm});
            skLineSegment(sketch, "E92.MirrorCS", {"start": v(94.05, 28.38) * mm, "end": v(94.05, -1.62) * mm});
            skLineSegment(sketch, "E93.MirrorCS", {"start": v(79.05, -1.62) * mm, "end": v(79.05, 10.38) * mm});
            skSolve(sketch);
        }
        {
            var Q0;
            Q0=makeQuery(id+"F16.imprint","IMPRINT",FACE,{"disambiguationData":[TD([[makeQuery(id+"F16.imprint","IMPRINT",EDGE,{"derivedFrom":makeQuery(id+"F1.opExtrude","CAP_EDGE",EDGE,{"disambiguationData":[OSD([sQuery(id+"F0.wireOp",EDGE,"E1.left")])],"isStart":true})}),-1.0]])]});
            var Q1;
            Q1=makeQuery(id+"F16.imprint","IMPRINT",FACE,{"disambiguationData":[TD([[makeQuery(id+"F16.imprint","IMPRINT",EDGE,{"derivedFrom":sQuery(id+"F16.wireOp",EDGE,"E80")}),-1.0]])]});
            var Q2;
            Q2=makeQuery(id+"F16.imprint","IMPRINT",FACE,{"disambiguationData":[TD([[makeQuery(id+"F16.imprint","IMPRINT",EDGE,{"derivedFrom":sQuery(id+"F16.wireOp",EDGE,"E87.MirrorCS")}),1.0]])]});
            extrude(context, id + "F17", {"entities" : qUnion([Q0, Q1, Q2]), "depth" : 3 * mm});
        }
    });
